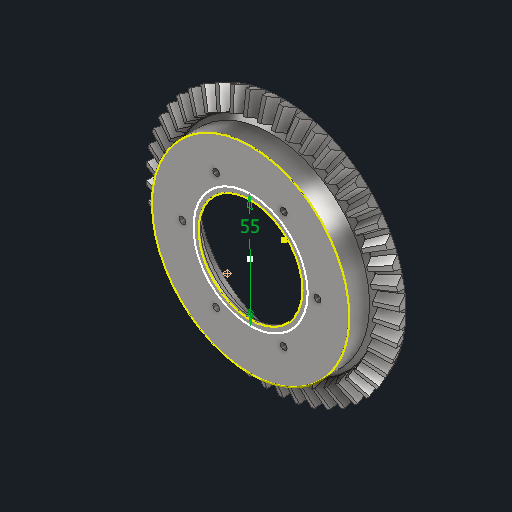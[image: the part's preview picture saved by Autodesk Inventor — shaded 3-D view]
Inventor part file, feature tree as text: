
AUTODESK INVENTOR PART (.ipt)
format: ipt  version: 2022 (Build 260153000, 153)  size: 913,408 bytes
history: native  units: mm
features: other x26, sketch x7, extrude x3, chamfer x3, projected_geometry x3, reference x3, loft x2, pattern_circular x2, hole x1
ambient origin geometry x6: Origin, XZ Plane, X Axis, Y Axis, Z Axis, Center Point
bodies: Solid1 (feature_tree)
feature tree (50):
  other  "Top Point"
  other  "Mesh Plane2"
  other  "Teeth Body"
  other  "Start Point"
  other  "Tooth Plane"
  other  "Start Sketch"
  other  "End Point"
  other  "3D Sketch Right"
  other  "End Plane Right"
  loft  "Loft Right"
  pattern_circular  "Circular Pattern Right"  [2 undecoded]
  other  "3D Sketch Left"
  other  "End Plane Left"
  loft  "Loft Left"
  pattern_circular  "Circular Pattern Left"  [2 undecoded]
  other  "Fix Body"
  sketch  "Sketch15"  dims[d2=121.840242mm]
  extrude  "Extrusion6"  Depth=10.0mm
  chamfer  "Chamfer3"  Distance=120.781755mm
  sketch  "Sketch17"  dims[d4=21.425483mm]
  extrude  "Extrusion7"  TaperAngle=0.0deg  [1 undecoded]
  extrude  "Extrusion8"  Depth=10.0mm TaperAngle=0.0deg
  chamfer  "Chamfer4"  Angle=360.0deg  [1 undecoded]
  chamfer  "Chamfer6"  Distance=428.686656mm
  hole  "Hole3"  [1 undecoded]
  sketch  "Sketch21"  dims[d8=55.203225mm d9=143.656013mm d11=10.275mm d12=47.611121mm d15=46.413249mm d16=120.781755mm d17=0.0mm d18=90.0deg d19=0.0mm d20=90.0deg d21=480.0mm d22=360.0deg d26=428.686656mm d27=3.781698mm d28=120.0mm d29=-11.938871mm d30=47.611121mm d31=46.413249mm d32=120.781755mm d35=0.0mm d37=0.0mm d39=0.0mm d40=90.0deg d41=480.0mm d42=360.0deg d46=90.0deg d47=90.0deg d48=0.0mm d49=0.0mm d50=90.0deg d51=0.654498mm d52=0.0mm d53=0.0mm d54=0.0mm d56=18.960921mm d57=167.172015mm d58=159.362015mm d59=140.553318mm d60=133.9869mm d61=140.553318mm d62=133.9869mm d65=428.686656mm d66=31.5mm d67=120.0mm d68=-11.938871mm d69=3.781698mm d70=46.413249mm d71=120.781755mm d72=47.611121mm d73=133.9869mm d74=140.553318mm d75=0.0mm d77=0.0mm d79=0.0mm d80=90.0deg d81=480.0mm d82=360.0deg d84=10.0mm d85=20.0mm d86=20.0mm d87=10.0mm d88=0.0mm d89=0.0mm d90=90.0deg d91=90.0deg d92=90.0deg d93=90.0deg d137=50.0mm d138=95.0mm d139=12.0mm d140=0.0mm d141=2.0mm d142=2.0mm d143=45.0deg d144=0.0mm d145=0.0mm d146=10.0mm d147=0.0mm d148=5.0mm d149=2.0mm d150=45.0deg d156=5.0mm d157=2.0mm d158=45.0deg d159=65.0mm d160=60.0mm d162=360.0deg d164=3.242mm d165=6.0mm d166=8.0mm d167=4.6mm d168=90.0deg d169=8.0mm d170=20.594885mm d171=55.0mm d95=0.5mm d96=0.872665mm d97=0.5mm d98=0.872665mm]
  other  "Mesh Plane"
  other  "Top Plane"
  other  "Teeth Body Sketch"
  other  "End Plane"
  other  "End Sketch"
  other  "Helical Curve Left"
  other  "End Sketch Left"
  other  "Body Sketch"
  sketch  "Sketch6"  dims[d0=120.0mm d1=117.791709mm]
  other  "Srf1"
  other  "Helical Curve Right"
  other  "End Sketch Right"
  projected_geometry  "Projected Loop5"
  sketch  "Sketch16"  dims[d3=10.0mm]
  projected_geometry  "Projected Loop6"
  sketch  "Sketch18"  dims[d5=90.0deg]
  reference  "Reference4"
  reference  "Reference5"
  reference  "Reference6"
  sketch  "Sketch20"  dims[d7=56.627956mm]
  projected_geometry  "Projected Loop7"
  other  "Pitch Diameter"
  other  "SistemaDeElevación.iam"
  other  "Tuerca2:1"
note: 7 required parameter values undecoded (feature->parameter linkage not recoverable at this tier; creation-order binding heuristic only, values carry confidence <= 0.55)
